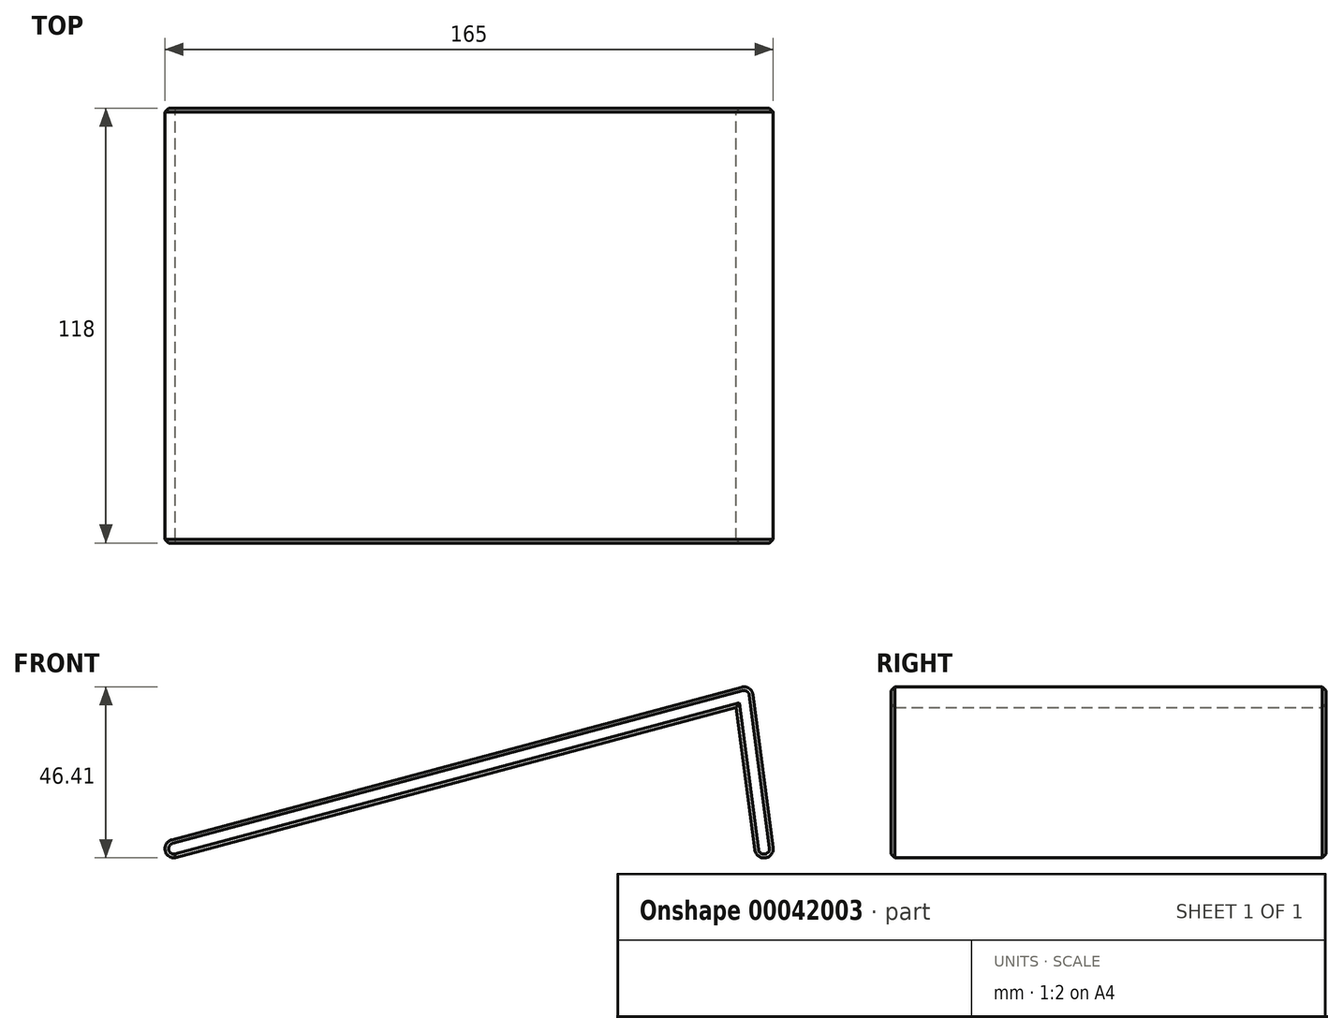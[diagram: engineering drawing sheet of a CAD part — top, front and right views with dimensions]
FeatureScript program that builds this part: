
annotation { "Feature Type Name" : "Feature", "Feature Type Description" : "" }
export const myFeature = defineFeature(function(context is Context, id is Id, definition is map)
    precondition{}
    {
        {
            var Q0;
            Q0=qCreatedBy(makeId("Front.planeOp"),FACE);
            var sketch = newSketch(context, id + "F0", { "sketchPlane" : qUnion([Q0])});
            skLineSegment(sketch, "E0", {"start": v(-12.32, 0) * mm, "end": v(-12, 0) * mm});
            skLineSegment(sketch, "E1", {"start": v(-12.97, 4.91) * mm, "end": v(141.58, 46.33) * mm});
            skLineSegment(sketch, "E2", {"start": v(144.7, 44.24) * mm, "end": v(150.15, 2.83) * mm});
            skPoint(sketch, "E3.visualSharp", {"position": v(144.33, 47.06) * mm});
            skArc(sketch, "E3.filletArc", {"start": v(144.7, 44.24) * mm, "mid": v(143.61, 45.99) * mm, "end": v(141.58, 46.33) * mm});
            skPoint(sketch, "E4.visualSharp", {"position": v(150.53, 0) * mm});
            skArc(sketch, "E4.filletArc", {"start": v(147.68, 0) * mm, "mid": v(149.55, 0.85) * mm, "end": v(150.15, 2.83) * mm});
            skPoint(sketch, "E5.visualSharp", {"position": v(-31.31, 0) * mm});
            skArc(sketch, "E5.filletArc", {"start": v(-12.97, 4.91) * mm, "mid": v(-14.8, 2.17) * mm, "end": v(-12.32, 0) * mm});
            skLineSegment(sketch, "E6.0", {"start": v(140.12, 40.76) * mm, "end": v(145.2, 2.17) * mm});
            skLineSegment(sketch, "E6.1", {"start": v(-12, 0) * mm, "end": v(140.12, 40.76) * mm});
            skLineSegment(sketch, "E7.trimOffspring", {"start": v(147.68, 0) * mm, "end": v(147.68, 0) * mm});
            skPoint(sketch, "E8.visualSharp", {"position": v(145.48, 0) * mm});
            skArc(sketch, "E8.filletArc", {"start": v(145.2, 2.17) * mm, "mid": v(146.03, 0.62) * mm, "end": v(147.68, 0) * mm});
            skSolve(sketch);
        }
        {
            var Q0;
            Q0=makeQuery(id+"F0.imprint","IMPRINT",FACE,{"disambiguationData":[TD([[makeQuery(id+"F0.imprint","IMPRINT",EDGE,{"derivedFrom":sQuery(id+"F0.wireOp",EDGE,"E0")}),1.0]])]});
            extrude(context, id + "F1", {"entities" : qUnion([Q0]), "depth" : 118 * mm});
        }
        {
            var Q0;
            Q0=makeQuery(id+"F1.opExtrude","CAP_FACE",FACE,{"disambiguationData":[OSD([sQuery(id+"F0.wireOp",EDGE,"E0"),sQuery(id+"F0.wireOp",EDGE,"E1"),sQuery(id+"F0.wireOp",EDGE,"E2"),sQuery(id+"F0.wireOp",EDGE,"E3.filletArc"),sQuery(id+"F0.wireOp",EDGE,"E4.filletArc"),sQuery(id+"F0.wireOp",EDGE,"E5.filletArc"),sQuery(id+"F0.wireOp",EDGE,"E6.0"),sQuery(id+"F0.wireOp",EDGE,"E6.1"),sQuery(id+"F0.wireOp",EDGE,"E6.2")])],"isStart":false});
            var Q1;
            Q1=makeQuery(id+"F1.opExtrude","CAP_FACE",FACE,{"disambiguationData":[OSD([sQuery(id+"F0.wireOp",EDGE,"E0"),sQuery(id+"F0.wireOp",EDGE,"E1"),sQuery(id+"F0.wireOp",EDGE,"E2"),sQuery(id+"F0.wireOp",EDGE,"E3.filletArc"),sQuery(id+"F0.wireOp",EDGE,"E4.filletArc"),sQuery(id+"F0.wireOp",EDGE,"E5.filletArc"),sQuery(id+"F0.wireOp",EDGE,"E6.0"),sQuery(id+"F0.wireOp",EDGE,"E6.1"),sQuery(id+"F0.wireOp",EDGE,"E6.2")])],"isStart":true});
            chamfer(context, id + "F2", {"entities" : qUnion([Q0, Q1]), "width" : 1 * mm, "tangentPropagation" : true});
        }
    });
